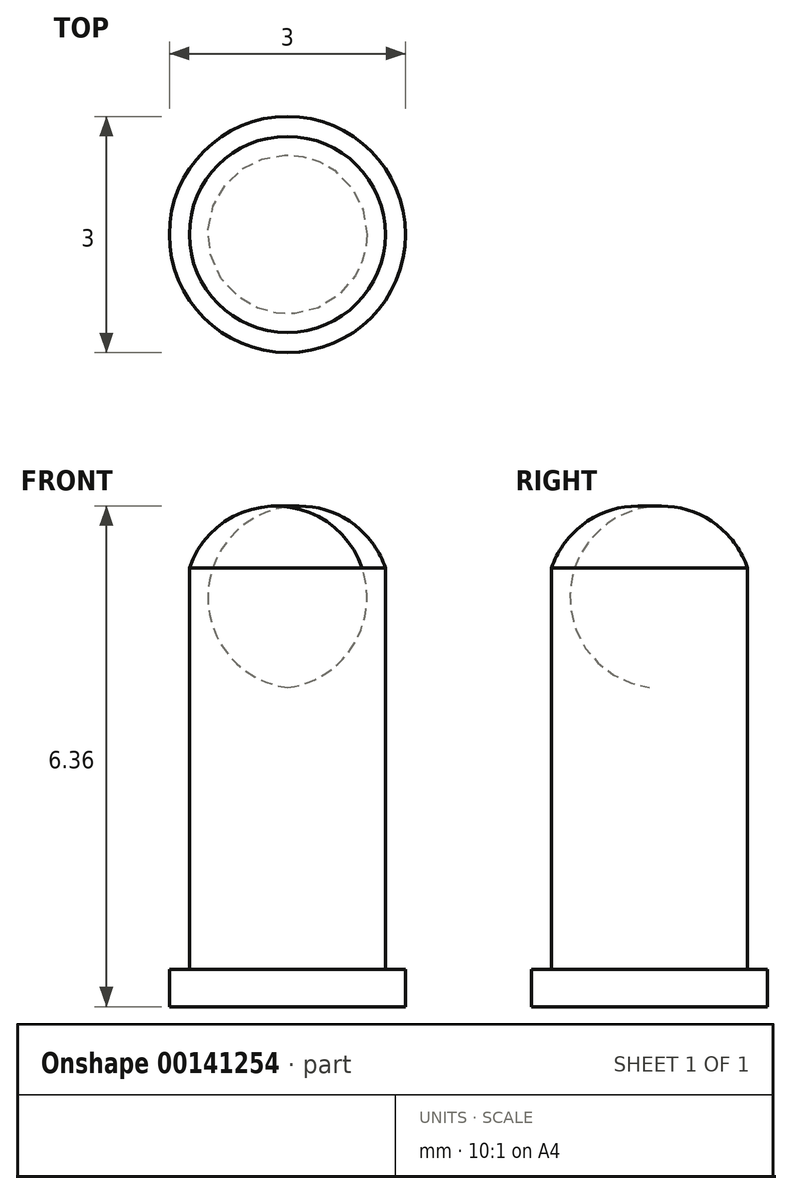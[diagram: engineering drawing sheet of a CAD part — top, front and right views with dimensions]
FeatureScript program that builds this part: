
annotation { "Feature Type Name" : "Feature", "Feature Type Description" : "" }
export const myFeature = defineFeature(function(context is Context, id is Id, definition is map)
    precondition{}
    {
        {
            var Q0;
            Q0=qCreatedBy(makeId("Front.planeOp"),FACE);
            var sketch = newSketch(context, id + "F0", { "sketchPlane" : qUnion([Q0])});
            skLineSegment(sketch, "E0", {"start": v(0, 0) * mm, "end": v(0, 6.35) * mm});
            skArc(sketch, "E1", {"start": v(1.25, 5.57) * mm, "mid": v(0.76, 6.18) * mm, "end": v(0, 6.35) * mm});
            skLineSegment(sketch, "E2", {"start": v(1.25, 5.57) * mm, "end": v(1.25, 0.48) * mm});
            skLineSegment(sketch, "E3", {"start": v(1.25, 0.48) * mm, "end": v(1.5, 0.48) * mm});
            skLineSegment(sketch, "E4", {"start": v(1.5, 0.48) * mm, "end": v(1.5, 0) * mm});
            skLineSegment(sketch, "E5", {"start": v(1.5, 0) * mm, "end": v(0, 0) * mm});
            skSolve(sketch);
        }
        {
            var Q0;
            Q0=makeQuery(id+"F0.imprint","IMPRINT",FACE,{"disambiguationData":[TD([[makeQuery(id+"F0.imprint","IMPRINT",EDGE,{"derivedFrom":sQuery(id+"F0.wireOp",EDGE,"E0")}),-1.0]])]});
            var Q1;
            Q1=sQuery(id+"F0.wireOp",EDGE,"E0");
            revolve(context, id + "F1", {"entities" : qUnion([Q0]), "axis" : qUnion([Q1]), "revolveType" : RevolveType.FULL});
        }
    });
